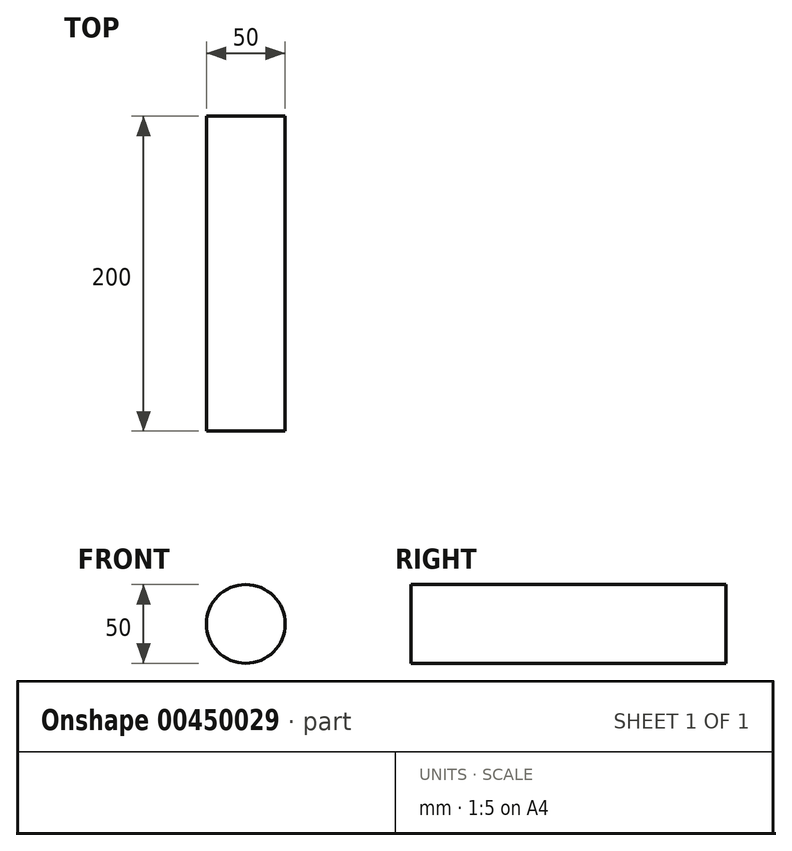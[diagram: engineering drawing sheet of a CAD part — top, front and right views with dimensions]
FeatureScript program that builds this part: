
annotation { "Feature Type Name" : "Feature", "Feature Type Description" : "" }
export const myFeature = defineFeature(function(context is Context, id is Id, definition is map)
    precondition{}
    {
        {
            var Q0;
            Q0=qCreatedBy(makeId("Front.planeOp"),FACE);
            var sketch = newSketch(context, id + "F0", { "sketchPlane" : qUnion([Q0])});
            skCircle(sketch, "E0", {"center": v(0, 0) * mm, "radius": 25 * mm});
            skSolve(sketch);
        }
        {
            var Q0;
            Q0=makeQuery(id+"F0.imprint","IMPRINT",FACE,{"disambiguationData":[TD([[makeQuery(id+"F0.imprint","IMPRINT",EDGE,{"derivedFrom":sQuery(id+"F0.wireOp",EDGE,"E0")}),1.0]])]});
            extrude(context, id + "F1", {"entities" : qUnion([Q0]), "depth" : 200 * mm});
        }
    });
